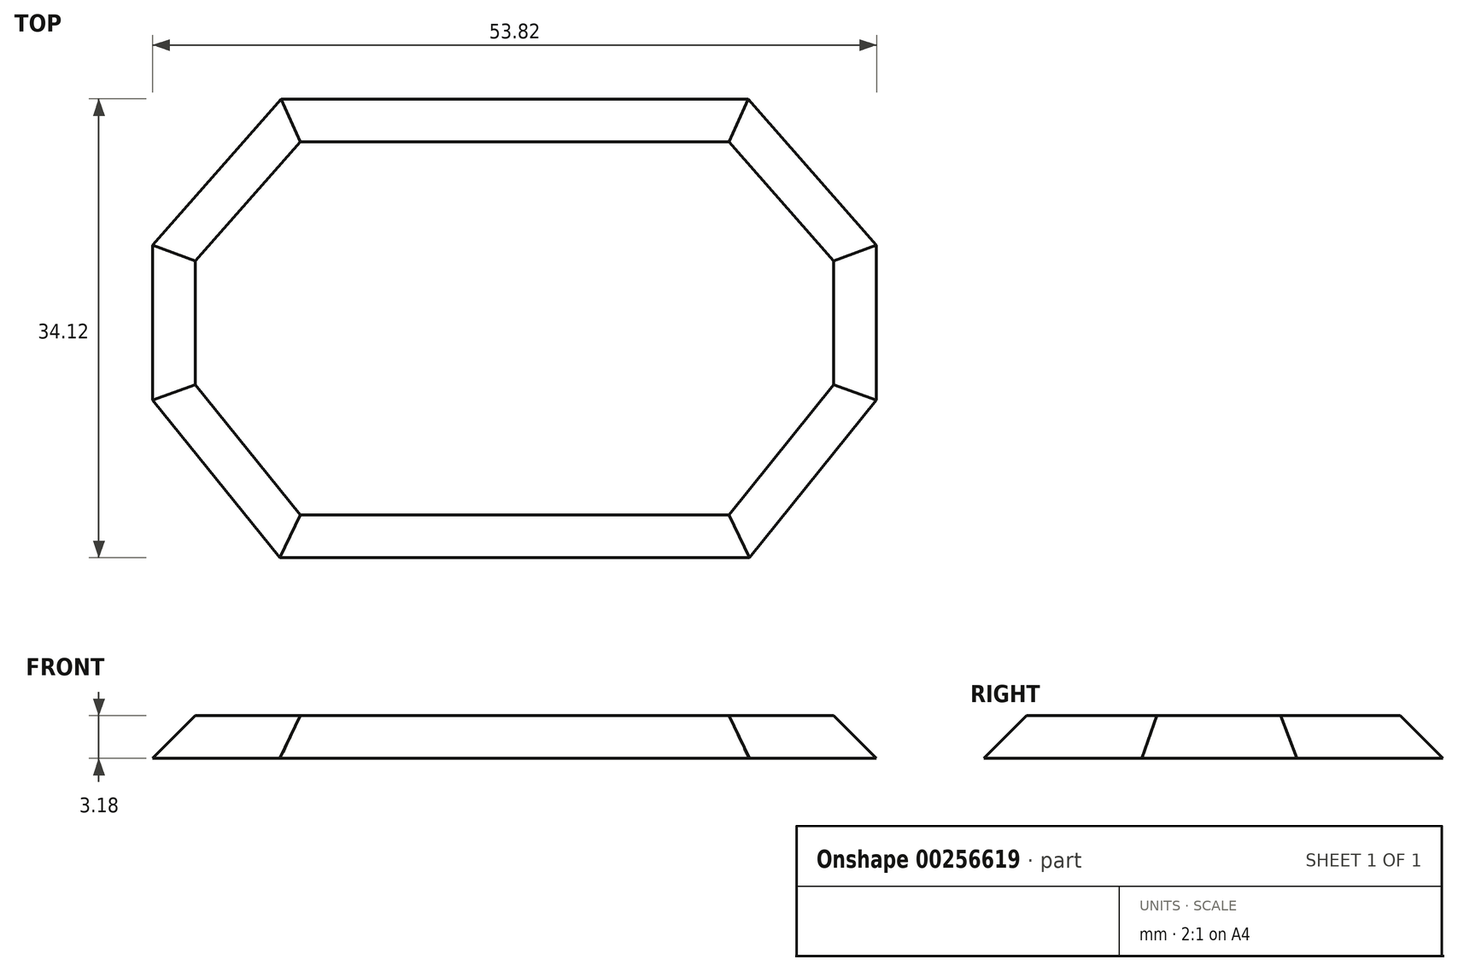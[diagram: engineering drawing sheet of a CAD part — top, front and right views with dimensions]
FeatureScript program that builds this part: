
annotation { "Feature Type Name" : "Feature", "Feature Type Description" : "" }
export const myFeature = defineFeature(function(context is Context, id is Id, definition is map)
    precondition{}
    {
        {
            var Q0;
            Q0=qCreatedBy(makeId("Top.planeOp"),FACE);
            var sketch = newSketch(context, id + "F0", { "sketchPlane" : qUnion([Q0])});
            skLineSegment(sketch, "E0.bottom", {"start": v(28.81, 18.96) * mm, "end": v(-28.81, 18.96) * mm});
            skLineSegment(sketch, "E0.top", {"start": v(28.81, -18.96) * mm, "end": v(-28.81, -18.96) * mm});
            skLineSegment(sketch, "E0.left", {"start": v(28.81, 18.96) * mm, "end": v(28.81, -18.96) * mm});
            skLineSegment(sketch, "E0.right", {"start": v(-28.81, 18.96) * mm, "end": v(-28.81, -18.96) * mm});
            skPoint(sketch, "E0.middle", {"position": v(0, 0) * mm});
            skLineSegment(sketch, "E1", {"start": v(-28.81, 6.9) * mm, "end": v(-18.23, 18.96) * mm});
            skLineSegment(sketch, "E2", {"start": v(28.81, 6.9) * mm, "end": v(18.23, 18.96) * mm});
            skLineSegment(sketch, "E3", {"start": v(-28.81, -6) * mm, "end": v(-18.38, -18.96) * mm});
            skLineSegment(sketch, "E4", {"start": v(28.81, -6) * mm, "end": v(18.38, -18.96) * mm});
            skSolve(sketch);
        }
        {
            var Q0;
            {var subQ0=sQuery(id+"F0.wireOp",EDGE,"E1");Q0=makeQuery(id+"F0.imprint","IMPRINT",FACE,{"disambiguationData":[TD([[makeQuery(id+"F0.imprint","IMPRINT",EDGE,{"derivedFrom":subQ0}),-1.0]])]});}
            extrude(context, id + "F1", {"entities" : qUnion([Q0]), "depth" : 3.17 * mm});
        }
        {
            var Q0;
            Q0=makeQuery(id+"F1.opExtrude","CAP_FACE",FACE,{"disambiguationData":[OSD([sQuery(id+"F0.wireOp",EDGE,"E0.bottom"),sQuery(id+"F0.wireOp",EDGE,"E0.top"),sQuery(id+"F0.wireOp",EDGE,"E0.left"),sQuery(id+"F0.wireOp",EDGE,"E0.right"),sQuery(id+"F0.wireOp",EDGE,"E1"),sQuery(id+"F0.wireOp",EDGE,"E2"),sQuery(id+"F0.wireOp",EDGE,"E3"),sQuery(id+"F0.wireOp",EDGE,"E4")])],"isStart":false});
            chamfer(context, id + "F2", {"entities" : qUnion([Q0]), "width" : 5.08 * mm, "tangentPropagation" : true});
        }
    });
